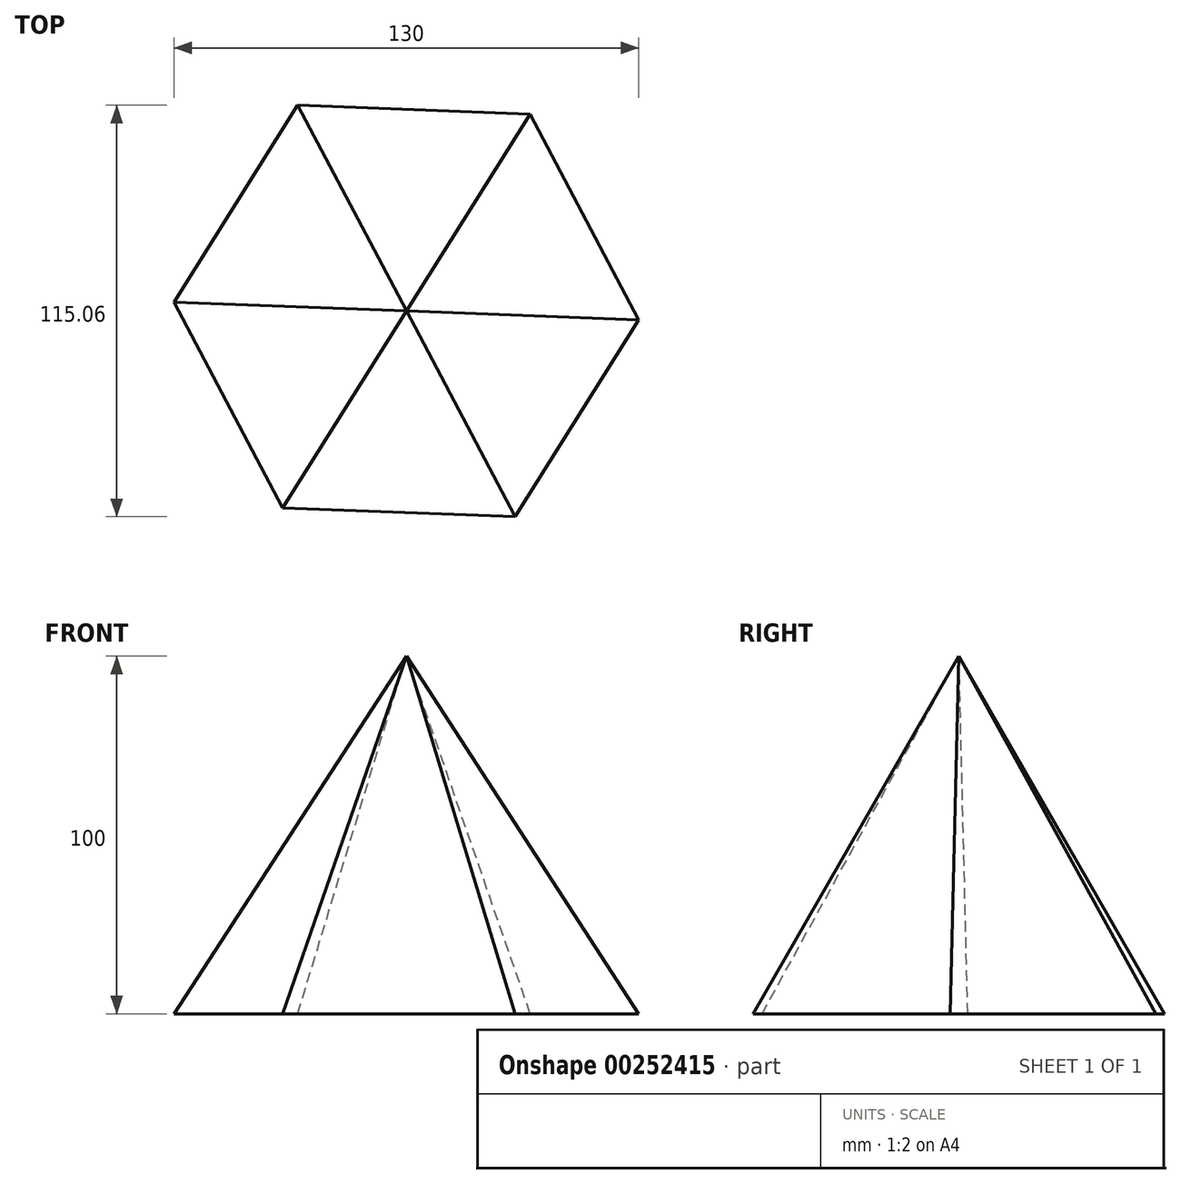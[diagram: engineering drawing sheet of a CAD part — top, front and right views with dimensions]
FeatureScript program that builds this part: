
annotation { "Feature Type Name" : "Feature", "Feature Type Description" : "" }
export const myFeature = defineFeature(function(context is Context, id is Id, definition is map)
    precondition{}
    {
        {
            var Q0;
            Q0=qCreatedBy(makeId("Top.planeOp"),FACE);
            var sketch = newSketch(context, id + "F0", { "sketchPlane" : qUnion([Q0])});
            skCircle(sketch, "E0.cCircle", {"center": v(0, 0) * mm, "radius": 65.05 * mm, "construction": true});
            skLineSegment(sketch, "E0.0", {"start": v(-65, 2.48) * mm, "end": v(-30.35, 57.53) * mm});
            skLineSegment(sketch, "E0.1", {"start": v(-30.35, 57.53) * mm, "end": v(34.65, 55.05) * mm});
            skLineSegment(sketch, "E0.2", {"start": v(34.65, 55.05) * mm, "end": v(65, -2.48) * mm});
            skLineSegment(sketch, "E0.3", {"start": v(65, -2.48) * mm, "end": v(30.35, -57.53) * mm});
            skLineSegment(sketch, "E0.4", {"start": v(30.35, -57.53) * mm, "end": v(-34.65, -55.05) * mm});
            skLineSegment(sketch, "E0.5", {"start": v(-34.65, -55.05) * mm, "end": v(-65, 2.48) * mm});
            skSolve(sketch);
        }
        {
            var Q0;
            Q0=qCreatedBy(makeId("Top.planeOp"),FACE);
            cPlane(context, id + "F1", {"entities" : qUnion([Q0]), "cplaneType" : CPlaneType.OFFSET, "offset" : 100 * mm, "width" : 152.4 * mm, "height" : 152.4 * mm});
        }
        {
            var Q0;
            Q0=qCreatedBy(id+"F1.planeOp",FACE);
            var sketch = newSketch(context, id + "F2", { "sketchPlane" : qUnion([Q0])});
            skPoint(sketch, "E1", {"position": v(0, 0) * mm});
            skSolve(sketch);
        }
        {
            var Q0;
            Q0=makeQuery(id+"F0.imprint","IMPRINT",FACE,{"disambiguationData":[TD([[makeQuery(id+"F0.imprint","IMPRINT",EDGE,{"derivedFrom":sQuery(id+"F0.wireOp",EDGE,"E0.0")}),-1.0]])]});
            var Q1;
            Q1=sQuery(id+"F2.wireOp",VERTEX,"E1");
            loft(context, id + "F3", {"sheetProfilesArray" : [{ "sheetProfileEntities" : qUnion([Q0]) }, { "sheetProfileEntities" : qUnion([Q1]) }]});
        }
    });
